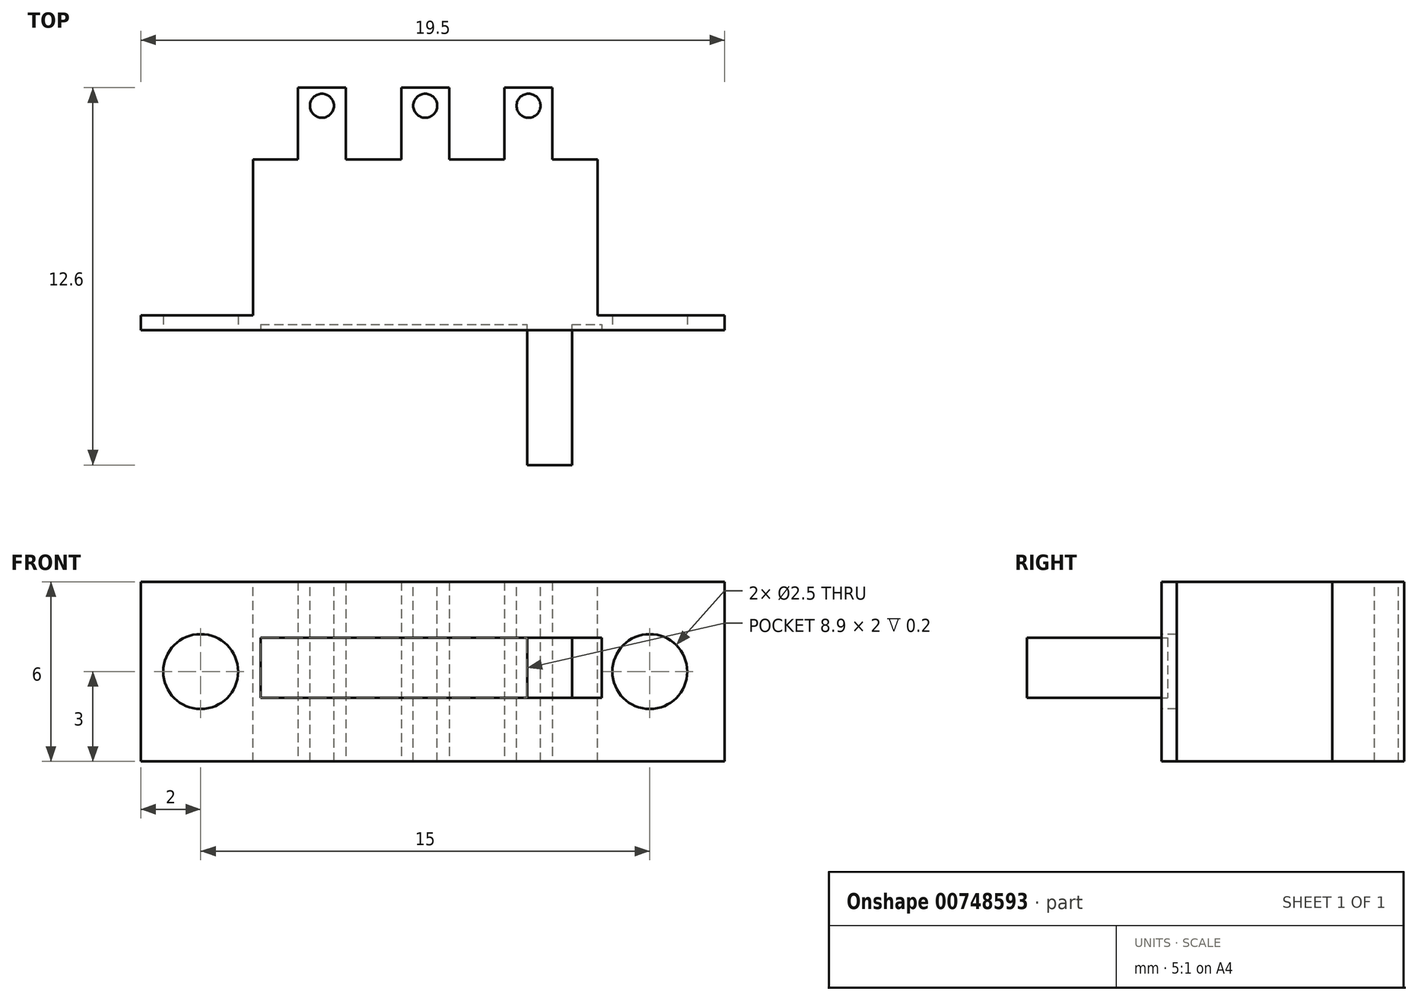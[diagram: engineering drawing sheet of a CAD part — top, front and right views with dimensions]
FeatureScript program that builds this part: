
annotation { "Feature Type Name" : "Feature", "Feature Type Description" : "" }
export const myFeature = defineFeature(function(context is Context, id is Id, definition is map)
    precondition{}
    {
        {
            var Q0;
            Q0=qCreatedBy(makeId("Front.planeOp"),FACE);
            var sketch = newSketch(context, id + "F0", { "sketchPlane" : qUnion([Q0])});
            skLineSegment(sketch, "E0.bottom", {"start": v(0, 0) * mm, "end": v(19.5, 0) * mm});
            skLineSegment(sketch, "E0.top", {"start": v(0, -6) * mm, "end": v(19.5, -6) * mm});
            skLineSegment(sketch, "E0.left", {"start": v(0, 0) * mm, "end": v(0, -6) * mm});
            skLineSegment(sketch, "E0.right", {"start": v(19.5, 0) * mm, "end": v(19.5, -6) * mm});
            skSolve(sketch);
        }
        {
            var Q0;
            Q0 = qSketchRegion(id + "F0", true);
            extrude(context, id + "F1", {"entities" : qUnion([Q0]), "depth" : 0.5 * mm, "offsetDistance" : 25 * mm});
        }
        {
            var Q0;
            Q0=makeQuery(id+"F1.opExtrude","CAP_FACE",FACE,{"disambiguationData":[OSD([sQuery(id+"F0.wireOp",EDGE,"E0.bottom"),sQuery(id+"F0.wireOp",EDGE,"E0.top"),sQuery(id+"F0.wireOp",EDGE,"E0.left"),sQuery(id+"F0.wireOp",EDGE,"E0.right")])],"isStart":false});
            var sketch = newSketch(context, id + "F2", { "sketchPlane" : qUnion([Q0])});
            skCircle(sketch, "E1", {"center": v(2, -3) * mm, "radius": 1.25 * mm});
            skPoint(sketch, "E1.centerSnap0", {"position": v(0, -3) * mm});
            skCircle(sketch, "E2", {"center": v(17, -3) * mm, "radius": 1.25 * mm});
            skSolve(sketch);
        }
        {
            var Q0;
            Q0 = qSketchRegion(id + "F2", true);
            extrude(context, id + "F3", {"entities" : qUnion([Q0]), "operationType" : NewBodyOperationType.REMOVE, "oppositeDirection" : true, "depth" : 3 * mm, "offsetDistance" : 25 * mm});
        }
        {
            var Q0;
            Q0=makeQuery(id+"F1.opExtrude","CAP_FACE",FACE,{"disambiguationData":[OSD([sQuery(id+"F0.wireOp",EDGE,"E0.bottom"),sQuery(id+"F0.wireOp",EDGE,"E0.top"),sQuery(id+"F0.wireOp",EDGE,"E0.left"),sQuery(id+"F0.wireOp",EDGE,"E0.right")])],"isStart":false});
            var sketch = newSketch(context, id + "F4", { "sketchPlane" : qUnion([Q0])});
            skLineSegment(sketch, "E3.bottom", {"start": v(4, -1.88) * mm, "end": v(15.4, -1.88) * mm});
            skLineSegment(sketch, "E3.top", {"start": v(4, -3.88) * mm, "end": v(15.4, -3.88) * mm});
            skLineSegment(sketch, "E3.left", {"start": v(4, -1.88) * mm, "end": v(4, -3.88) * mm});
            skLineSegment(sketch, "E3.right", {"start": v(15.4, -1.88) * mm, "end": v(15.4, -3.88) * mm});
            skSolve(sketch);
        }
        {
            var Q0;
            Q0 = qSketchRegion(id + "F4", true);
            extrude(context, id + "F5", {"entities" : qUnion([Q0]), "operationType" : NewBodyOperationType.REMOVE, "oppositeDirection" : true, "depth" : 0.2 * mm, "offsetDistance" : 25 * mm});
        }
        {
            var Q0;
            Q0=makeQuery(id+"F5.boolean.opBoolean","COPY",FACE,{"derivedFrom":makeQuery(id+"F5.opExtrude","CAP_FACE",FACE,{"disambiguationData":[OSD([sQuery(id+"F4.wireOp",EDGE,"E3.bottom"),sQuery(id+"F4.wireOp",EDGE,"E3.top"),sQuery(id+"F4.wireOp",EDGE,"E3.left"),sQuery(id+"F4.wireOp",EDGE,"E3.right")])],"isStart":false})});
            var sketch = newSketch(context, id + "F6", { "sketchPlane" : qUnion([Q0])});
            skLineSegment(sketch, "E4.bottom", {"start": v(14.4, -1.88) * mm, "end": v(12.9, -1.88) * mm});
            skLineSegment(sketch, "E4.top", {"start": v(14.4, -3.88) * mm, "end": v(12.9, -3.88) * mm});
            skLineSegment(sketch, "E4.left", {"start": v(14.4, -1.88) * mm, "end": v(14.4, -3.88) * mm});
            skLineSegment(sketch, "E4.right", {"start": v(12.9, -1.88) * mm, "end": v(12.9, -3.88) * mm});
            skSolve(sketch);
        }
        {
            var Q0;
            Q0 = qSketchRegion(id + "F6", true);
            extrude(context, id + "F7", {"entities" : qUnion([Q0]), "operationType" : NewBodyOperationType.ADD, "depth" : 4.7 * mm, "offsetDistance" : 25 * mm});
        }
        {
            var Q0;
            Q0=makeQuery(id+"F1.opExtrude","CAP_FACE",FACE,{"disambiguationData":[OSD([sQuery(id+"F0.wireOp",EDGE,"E0.bottom"),sQuery(id+"F0.wireOp",EDGE,"E0.top"),sQuery(id+"F0.wireOp",EDGE,"E0.left"),sQuery(id+"F0.wireOp",EDGE,"E0.right")])],"isStart":true});
            var sketch = newSketch(context, id + "F8", { "sketchPlane" : qUnion([Q0])});
            skLineSegment(sketch, "E5.bottom", {"start": v(-15.25, -6) * mm, "end": v(-3.75, -6) * mm});
            skLineSegment(sketch, "E5.top", {"start": v(-15.25, 0) * mm, "end": v(-3.75, 0) * mm});
            skLineSegment(sketch, "E5.left", {"start": v(-15.25, -6) * mm, "end": v(-15.25, 0) * mm});
            skLineSegment(sketch, "E5.right", {"start": v(-3.75, -6) * mm, "end": v(-3.75, 0) * mm});
            skSolve(sketch);
        }
        {
            var Q0;
            Q0 = qSketchRegion(id + "F8", true);
            extrude(context, id + "F9", {"entities" : qUnion([Q0]), "operationType" : NewBodyOperationType.ADD, "depth" : 5.2 * mm, "offsetDistance" : 25 * mm});
        }
        {
            var Q0;
            Q0=makeQuery(id+"F9.opExtrude","CAP_FACE",FACE,{"disambiguationData":[OSD([sQuery(id+"F8.wireOp",EDGE,"E5.bottom"),sQuery(id+"F8.wireOp",EDGE,"E5.top"),sQuery(id+"F8.wireOp",EDGE,"E5.left"),sQuery(id+"F8.wireOp",EDGE,"E5.right")])],"isStart":false});
            var sketch = newSketch(context, id + "F10", { "sketchPlane" : qUnion([Q0])});
            skLineSegment(sketch, "E6.bottom", {"start": v(-13.75, 0) * mm, "end": v(-12.15, 0) * mm});
            skLineSegment(sketch, "E6.top", {"start": v(-13.75, -6) * mm, "end": v(-12.15, -6) * mm});
            skLineSegment(sketch, "E6.left", {"start": v(-13.75, 0) * mm, "end": v(-13.75, -6) * mm});
            skLineSegment(sketch, "E6.right", {"start": v(-12.15, 0) * mm, "end": v(-12.15, -6) * mm});
            skLineSegment(sketch, "E7.bottom", {"start": v(-10.3, 0) * mm, "end": v(-8.7, 0) * mm});
            skLineSegment(sketch, "E7.top", {"start": v(-10.3, -6) * mm, "end": v(-8.7, -6) * mm});
            skLineSegment(sketch, "E7.left", {"start": v(-10.3, 0) * mm, "end": v(-10.3, -6) * mm});
            skLineSegment(sketch, "E7.right", {"start": v(-8.7, 0) * mm, "end": v(-8.7, -6) * mm});
            skLineSegment(sketch, "E8.bottom", {"start": v(-6.85, 0) * mm, "end": v(-5.25, 0) * mm});
            skLineSegment(sketch, "E8.top", {"start": v(-6.85, -6) * mm, "end": v(-5.25, -6) * mm});
            skLineSegment(sketch, "E8.left", {"start": v(-6.85, 0) * mm, "end": v(-6.85, -6) * mm});
            skLineSegment(sketch, "E8.right", {"start": v(-5.25, 0) * mm, "end": v(-5.25, -6) * mm});
            skSolve(sketch);
        }
        {
            var Q0;
            Q0 = qSketchRegion(id + "F10", true);
            extrude(context, id + "F11", {"entities" : qUnion([Q0]), "operationType" : NewBodyOperationType.ADD, "depth" : 2.4 * mm, "offsetDistance" : 25 * mm});
        }
        {
            var Q0;
            Q0=makeQuery(id+"F11.boolean.opBoolean","MERGE",FACE,{"derivedFrom":[makeQuery(id+"F9.boolean.opBoolean","MERGE",FACE,{"derivedFrom":[makeQuery(id+"F1.opExtrude","SWEPT_FACE",FACE,{"disambiguationData":[OSD([sQuery(id+"F0.wireOp",EDGE,"E0.bottom")])]}),makeQuery(id+"F9.opExtrude","SWEPT_FACE",FACE,{"disambiguationData":[OSD([sQuery(id+"F8.wireOp",EDGE,"E5.top")])]})]}),makeQuery(id+"F11.opExtrude","SWEPT_FACE",FACE,{"disambiguationData":[OSD([sQuery(id+"F10.wireOp",EDGE,"E6.bottom")])]}),makeQuery(id+"F11.opExtrude","SWEPT_FACE",FACE,{"disambiguationData":[OSD([sQuery(id+"F10.wireOp",EDGE,"E7.bottom")])]}),makeQuery(id+"F11.opExtrude","SWEPT_FACE",FACE,{"disambiguationData":[OSD([sQuery(id+"F10.wireOp",EDGE,"E8.bottom")])]})]});
            var sketch = newSketch(context, id + "F12", { "sketchPlane" : qUnion([Q0])});
            skCircle(sketch, "E9", {"center": v(12.95, 7) * mm, "radius": 0.4 * mm});
            skCircle(sketch, "E10", {"center": v(9.5, 7) * mm, "radius": 0.4 * mm});
            skCircle(sketch, "E11", {"center": v(6.05, 7) * mm, "radius": 0.4 * mm});
            skSolve(sketch);
        }
        {
            var Q0;
            Q0 = qSketchRegion(id + "F12", true);
            extrude(context, id + "F13", {"entities" : qUnion([Q0]), "operationType" : NewBodyOperationType.REMOVE, "oppositeDirection" : true, "depth" : 6 * mm, "offsetDistance" : 25 * mm});
        }
    });
